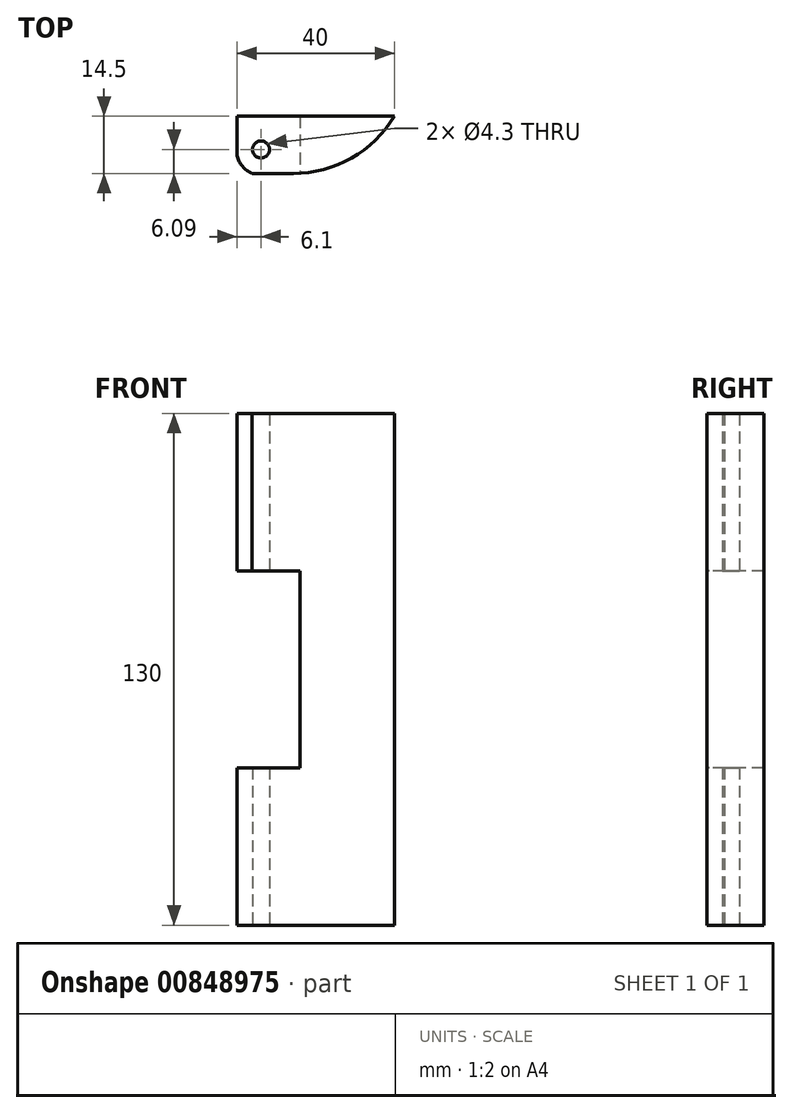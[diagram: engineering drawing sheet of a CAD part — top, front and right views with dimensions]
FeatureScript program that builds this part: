
annotation { "Feature Type Name" : "Feature", "Feature Type Description" : "" }
export const myFeature = defineFeature(function(context is Context, id is Id, definition is map)
    precondition{}
    {
        {
            var Q0;
            Q0=qCreatedBy(makeId("Top.planeOp"),FACE);
            var sketch = newSketch(context, id + "F0", { "sketchPlane" : qUnion([Q0])});
            skLineSegment(sketch, "E0.bottom", {"start": v(6.1, 8.41) * mm, "end": v(-6.1, 8.41) * mm});
            skLineSegment(sketch, "E0.left", {"start": v(6.1, 8.41) * mm, "end": v(6.1, -1.59) * mm});
            skLineSegment(sketch, "E0.right", {"start": v(-6.1, 8.41) * mm, "end": v(-6.1, -1.59) * mm});
            skArc(sketch, "E1", {"start": v(-6.1, -1.59) * mm, "mid": v(-4.7, -4.3) * mm, "end": v(-2.25, -6.09) * mm});
            skLineSegment(sketch, "E2", {"start": v(-2.25, -6.1) * mm, "end": v(0, -6.1) * mm});
            skArc(sketch, "E3.MirrorCS", {"start": v(6.1, -1.59) * mm, "mid": v(4.7, -4.3) * mm, "end": v(2.25, -6.09) * mm});
            skLineSegment(sketch, "E4.MirrorCS", {"start": v(2.25, -6.09) * mm, "end": v(0, -6.1) * mm});
            skCircle(sketch, "E5", {"center": v(0, 0) * mm, "radius": 2.15 * mm});
            skLineSegment(sketch, "E6.bottom", {"start": v(0, -6.1) * mm, "end": v(33.9, -6.1) * mm});
            skLineSegment(sketch, "E6.top", {"start": v(0, 8.41) * mm, "end": v(33.9, 8.41) * mm});
            skLineSegment(sketch, "E6.left", {"start": v(0, -6.1) * mm, "end": v(0, 8.41) * mm});
            skLineSegment(sketch, "E6.right", {"start": v(33.9, -6.1) * mm, "end": v(33.9, 8.41) * mm});
            skPoint(sketch, "E7", {"position": v(9.9, 8.41) * mm});
            skLineSegment(sketch, "E8", {"start": v(9.9, 8.41) * mm, "end": v(9.9, -6.1) * mm});
            skSolve(sketch);
        }
        {
            var Q0;
            {var subQ0=sQuery(id+"F0.wireOp",EDGE,"E6.right");Q0=makeQuery(id+"F0.imprint","IMPRINT",FACE,{"disambiguationData":[TD([[makeQuery(id+"F0.imprint","IMPRINT",EDGE,{"derivedFrom":subQ0}),1.0]])]});}
            extrude(context, id + "F1", {"entities" : qUnion([Q0]), "depth" : (40 + 50 + 40) * mm, "offsetDistance" : 25 * mm});
        }
        {
            var Q0;
            {var subQ1=sQuery(id+"F0.wireOp",EDGE,"E0.left");Q0=makeQuery(id+"F0.imprint","IMPRINT",FACE,{"disambiguationData":[TD([[makeQuery(id+"F0.imprint","IMPRINT",EDGE,{"derivedFrom":subQ1}),1.0]])]});}
            var Q1;
            {var subQ9=sQuery(id+"F0.wireOp",EDGE,"E0.left");Q1=makeQuery(id+"F0.imprint","IMPRINT",FACE,{"disambiguationData":[TD([[makeQuery(id+"F0.imprint","IMPRINT",EDGE,{"derivedFrom":subQ9}),-1.0]])]});}
            var Q2;
            {var subQ4=sQuery(id+"F0.wireOp",EDGE,"E0.bottom");Q2=makeQuery(id+"F0.imprint","IMPRINT",FACE,{"disambiguationData":[TD([[makeQuery(id+"F0.imprint","IMPRINT",EDGE,{"derivedFrom":subQ4}),1.0]])]});}
            extrude(context, id + "F2", {"entities" : qUnion([Q0, Q1, Q2]), "operationType" : NewBodyOperationType.ADD, "depth" : (40 + 50 + 40) * mm, "offsetDistance" : 25 * mm});
        }
        {
            var Q0;
            {var subQ1=sQuery(id+"F0.wireOp",EDGE,"E0.left");Q0=makeQuery(id+"F0.imprint","IMPRINT",FACE,{"disambiguationData":[TD([[makeQuery(id+"F0.imprint","IMPRINT",EDGE,{"derivedFrom":subQ1}),1.0]])]});}
            var Q1;
            {var subQ9=sQuery(id+"F0.wireOp",EDGE,"E0.left");Q1=makeQuery(id+"F0.imprint","IMPRINT",FACE,{"disambiguationData":[TD([[makeQuery(id+"F0.imprint","IMPRINT",EDGE,{"derivedFrom":subQ9}),-1.0]])]});}
            var Q2;
            {var subQ4=sQuery(id+"F0.wireOp",EDGE,"E0.bottom");Q2=makeQuery(id+"F0.imprint","IMPRINT",FACE,{"disambiguationData":[TD([[makeQuery(id+"F0.imprint","IMPRINT",EDGE,{"derivedFrom":subQ4}),1.0]])]});}
            extrude(context, id + "F3", {"entities" : qUnion([Q0, Q1, Q2]), "operationType" : NewBodyOperationType.REMOVE, "depth" : (40 + 50) * mm, "offsetDistance" : 25 * mm});
        }
        {
            var Q0;
            Q0=makeQuery(id+"F0.imprint","IMPRINT",FACE,{"disambiguationData":[TD([[makeQuery(id+"F0.imprint","IMPRINT",EDGE,{"derivedFrom":sQuery(id+"F0.wireOp",EDGE,"E0.bottom")}),1.0]])]});
            var Q1;
            {var subQ7=sQuery(id+"F0.wireOp",EDGE,"E0.left");Q1=makeQuery(id+"F0.imprint","IMPRINT",FACE,{"disambiguationData":[TD([[makeQuery(id+"F0.imprint","IMPRINT",EDGE,{"derivedFrom":subQ7}),-1.0]])]});}
            var Q2;
            {var subQ4=sQuery(id+"F0.wireOp",EDGE,"E0.left");Q2=makeQuery(id+"F0.imprint","IMPRINT",FACE,{"disambiguationData":[TD([[makeQuery(id+"F0.imprint","IMPRINT",EDGE,{"derivedFrom":subQ4}),1.0]])]});}
            extrude(context, id + "F4", {"entities" : qUnion([Q0, Q1, Q2]), "operationType" : NewBodyOperationType.ADD, "depth" : 40 * mm, "offsetDistance" : 25 * mm});
        }
        {
            var Q0;
            Q0=makeQuery(id+"F4.opExtrude","SWEPT_EDGE",EDGE,{"disambiguationData":[OSD([sQuery(id+"F0.wireOp",EDGE,"E1"),sQuery(id+"F0.wireOp",EDGE,"E2")])]});
            var Q1;
            Q1=makeQuery(id+"F4.opExtrude","SWEPT_EDGE",EDGE,{"disambiguationData":[OSD([sQuery(id+"F0.wireOp",EDGE,"E3.MirrorCS"),sQuery(id+"F0.wireOp",EDGE,"E4.MirrorCS")])]});
            fillet(context, id + "F5", {"entities" : qUnion([Q0, Q1]), "radius" : 1 * mm, "tangentPropagation" : true, "allowEdgeOverflow" : false});
        }
        {
            var Q0;
            Q0=makeQuery(id+"F1.opExtrude","SWEPT_EDGE",EDGE,{"disambiguationData":[OSD([sQuery(id+"F0.wireOp",EDGE,"E6.bottom"),sQuery(id+"F0.wireOp",EDGE,"E6.right")])]});
            fillet(context, id + "F6", {"entities" : qUnion([Q0]), "radius" : 30 * mm, "tangentPropagation" : true, "allowEdgeOverflow" : false});
        }
    });
